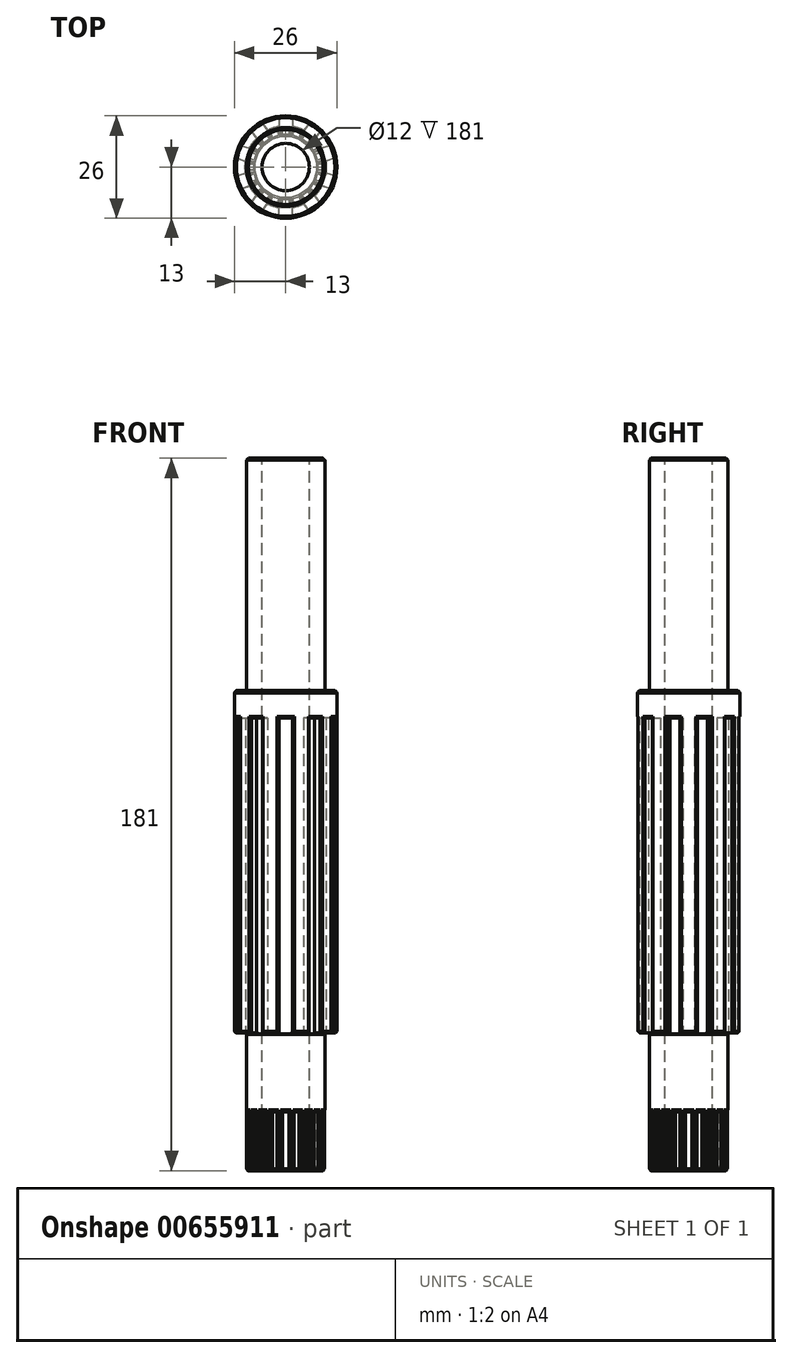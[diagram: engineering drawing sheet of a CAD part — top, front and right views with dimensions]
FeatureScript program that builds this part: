
annotation { "Feature Type Name" : "Feature", "Feature Type Description" : "" }
export const myFeature = defineFeature(function(context is Context, id is Id, definition is map)
    precondition{}
    {
        {
            var Q0;
            Q0=qCreatedBy(makeId("Top.planeOp"),FACE);
            var sketch = newSketch(context, id + "F0", { "sketchPlane" : qUnion([Q0])});
            skCircle(sketch, "E0", {"center": v(0, 0) * mm, "radius": 10 * mm});
            skSolve(sketch);
        }
        {
            var Q0;
            Q0=makeQuery(id+"F0.imprint","IMPRINT",FACE,{"disambiguationData":[TD([[makeQuery(id+"F0.imprint","IMPRINT",EDGE,{"derivedFrom":sQuery(id+"F0.wireOp",EDGE,"E0")}),1.0]])]});
            extrude(context, id + "F1", {"entities" : qUnion([Q0]), "oppositeDirection" : true, "depth" : 59 * mm, "offsetDistance" : 25 * mm});
        }
        {
            var Q0;
            Q0=makeQuery(id+"F1.opExtrude","CAP_FACE",FACE,{"disambiguationData":[OSD([sQuery(id+"F0.wireOp",EDGE,"E0")])],"isStart":false});
            var sketch = newSketch(context, id + "F2", { "sketchPlane" : qUnion([Q0])});
            skCircle(sketch, "E1", {"center": v(0, 0) * mm, "radius": 13 * mm});
            skSolve(sketch);
        }
        {
            var Q0;
            Q0=makeQuery(id+"F2.imprint","IMPRINT",FACE,{"disambiguationData":[TD([[makeQuery(id+"F2.imprint","IMPRINT",EDGE,{"derivedFrom":makeQuery(id+"F1.opExtrude","CAP_EDGE",EDGE,{"disambiguationData":[OSD([sQuery(id+"F0.wireOp",EDGE,"E0")])],"isStart":false})}),-1.0]])]});
            var Q1;
            Q1=makeQuery(id+"F2.imprint","IMPRINT",FACE,{"disambiguationData":[TD([[makeQuery(id+"F2.imprint","IMPRINT",EDGE,{"derivedFrom":sQuery(id+"F2.wireOp",EDGE,"E1")}),1.0]])]});
            var Q2;
            Q2=sQuery(id+"F2.wireOp",EDGE,"E1");
            extrude(context, id + "F3", {"entities" : qUnion([Q0, Q1]), "operationType" : NewBodyOperationType.ADD, "surfaceEntities" : qUnion([Q2]), "depth" : 87 * mm, "offsetDistance" : 25 * mm});
        }
        {
            var Q0;
            Q0=makeQuery(id+"F3.opExtrude","CAP_FACE",FACE,{"disambiguationData":[OSD([sQuery(id+"F2.wireOp",EDGE,"E1")])],"isStart":false});
            var sketch = newSketch(context, id + "F4", { "sketchPlane" : qUnion([Q0])});
            skLineSegment(sketch, "E2.bottom", {"start": v(1.73, 13.86) * mm, "end": v(-1.73, 13.86) * mm});
            skLineSegment(sketch, "E2.top", {"start": v(1.73, 10.15) * mm, "end": v(-1.73, 10.15) * mm});
            skLineSegment(sketch, "E2.left", {"start": v(1.73, 13.86) * mm, "end": v(1.73, 10.15) * mm});
            skLineSegment(sketch, "E2.right", {"start": v(-1.73, 13.86) * mm, "end": v(-1.73, 10.15) * mm});
            skPoint(sketch, "E2.middle", {"position": v(0, 12) * mm});
            skLineSegment(sketch, "E3.1.0", {"start": v(-9.54, 10.2) * mm, "end": v(-7.36, 7.2) * mm});
            skLineSegment(sketch, "E3.1.1", {"start": v(-6.75, 12.23) * mm, "end": v(-4.57, 9.23) * mm});
            skLineSegment(sketch, "E3.1.2", {"start": v(-4.57, 9.23) * mm, "end": v(-7.36, 7.2) * mm});
            skLineSegment(sketch, "E3.1.3", {"start": v(-6.75, 12.23) * mm, "end": v(-9.54, 10.2) * mm});
            skLineSegment(sketch, "E3.2.0", {"start": v(-13.72, 2.64) * mm, "end": v(-10.19, 1.5) * mm});
            skLineSegment(sketch, "E3.2.1", {"start": v(-12.65, 5.93) * mm, "end": v(-9.12, 4.78) * mm});
            skLineSegment(sketch, "E3.2.2", {"start": v(-9.12, 4.78) * mm, "end": v(-10.19, 1.5) * mm});
            skLineSegment(sketch, "E3.2.3", {"start": v(-12.65, 5.93) * mm, "end": v(-13.72, 2.64) * mm});
            skLineSegment(sketch, "E3.3.0", {"start": v(-12.65, -5.93) * mm, "end": v(-9.12, -4.78) * mm});
            skLineSegment(sketch, "E3.3.1", {"start": v(-13.72, -2.64) * mm, "end": v(-10.19, -1.5) * mm});
            skLineSegment(sketch, "E3.3.2", {"start": v(-10.19, -1.5) * mm, "end": v(-9.12, -4.78) * mm});
            skLineSegment(sketch, "E3.3.3", {"start": v(-13.72, -2.64) * mm, "end": v(-12.65, -5.93) * mm});
            skLineSegment(sketch, "E3.4.0", {"start": v(-6.75, -12.23) * mm, "end": v(-4.57, -9.23) * mm});
            skLineSegment(sketch, "E3.4.1", {"start": v(-9.54, -10.2) * mm, "end": v(-7.36, -7.2) * mm});
            skLineSegment(sketch, "E3.4.2", {"start": v(-7.36, -7.2) * mm, "end": v(-4.57, -9.23) * mm});
            skLineSegment(sketch, "E3.4.3", {"start": v(-9.54, -10.2) * mm, "end": v(-6.75, -12.23) * mm});
            skLineSegment(sketch, "E3.5.0", {"start": v(1.73, -13.86) * mm, "end": v(1.73, -10.15) * mm});
            skLineSegment(sketch, "E3.5.1", {"start": v(-1.73, -13.86) * mm, "end": v(-1.73, -10.15) * mm});
            skLineSegment(sketch, "E3.5.2", {"start": v(-1.73, -10.15) * mm, "end": v(1.73, -10.15) * mm});
            skLineSegment(sketch, "E3.5.3", {"start": v(-1.73, -13.86) * mm, "end": v(1.73, -13.86) * mm});
            skLineSegment(sketch, "E3.6.0", {"start": v(9.54, -10.2) * mm, "end": v(7.36, -7.2) * mm});
            skLineSegment(sketch, "E3.6.1", {"start": v(6.75, -12.23) * mm, "end": v(4.57, -9.23) * mm});
            skLineSegment(sketch, "E3.6.2", {"start": v(4.57, -9.23) * mm, "end": v(7.36, -7.2) * mm});
            skLineSegment(sketch, "E3.6.3", {"start": v(6.75, -12.23) * mm, "end": v(9.54, -10.2) * mm});
            skLineSegment(sketch, "E3.7.0", {"start": v(13.72, -2.64) * mm, "end": v(10.19, -1.5) * mm});
            skLineSegment(sketch, "E3.7.1", {"start": v(12.65, -5.93) * mm, "end": v(9.12, -4.78) * mm});
            skLineSegment(sketch, "E3.7.2", {"start": v(9.12, -4.78) * mm, "end": v(10.19, -1.5) * mm});
            skLineSegment(sketch, "E3.7.3", {"start": v(12.65, -5.93) * mm, "end": v(13.72, -2.64) * mm});
            skLineSegment(sketch, "E3.8.0", {"start": v(12.65, 5.93) * mm, "end": v(9.12, 4.78) * mm});
            skLineSegment(sketch, "E3.8.1", {"start": v(13.72, 2.64) * mm, "end": v(10.19, 1.5) * mm});
            skLineSegment(sketch, "E3.8.2", {"start": v(10.19, 1.5) * mm, "end": v(9.12, 4.78) * mm});
            skLineSegment(sketch, "E3.8.3", {"start": v(13.72, 2.64) * mm, "end": v(12.65, 5.93) * mm});
            skLineSegment(sketch, "E3.9.0", {"start": v(6.75, 12.23) * mm, "end": v(4.57, 9.23) * mm});
            skLineSegment(sketch, "E3.9.1", {"start": v(9.54, 10.2) * mm, "end": v(7.36, 7.2) * mm});
            skLineSegment(sketch, "E3.9.2", {"start": v(7.36, 7.2) * mm, "end": v(4.57, 9.23) * mm});
            skLineSegment(sketch, "E3.9.3", {"start": v(9.54, 10.2) * mm, "end": v(6.75, 12.23) * mm});
            skPoint(sketch, "E3.center", {"position": v(0, 0) * mm});
            skSolve(sketch);
        }
        {
            var Q0;
            {var subQ0=sQuery(id+"F4.wireOp",EDGE,"E3.1.2");Q0=makeQuery(id+"F4.imprint","IMPRINT",FACE,{"disambiguationData":[TD([[makeQuery(id+"F4.imprint","IMPRINT",EDGE,{"derivedFrom":subQ0}),-1.0]])]});}
            var Q1;
            {var subQ0=sQuery(id+"F4.wireOp",EDGE,"E3.2.2");Q1=makeQuery(id+"F4.imprint","IMPRINT",FACE,{"disambiguationData":[TD([[makeQuery(id+"F4.imprint","IMPRINT",EDGE,{"derivedFrom":subQ0}),-1.0]])]});}
            var Q2;
            {var subQ0=sQuery(id+"F4.wireOp",EDGE,"E3.3.2");Q2=makeQuery(id+"F4.imprint","IMPRINT",FACE,{"disambiguationData":[TD([[makeQuery(id+"F4.imprint","IMPRINT",EDGE,{"derivedFrom":subQ0}),-1.0]])]});}
            var Q3;
            {var subQ0=sQuery(id+"F4.wireOp",EDGE,"E3.4.2");Q3=makeQuery(id+"F4.imprint","IMPRINT",FACE,{"disambiguationData":[TD([[makeQuery(id+"F4.imprint","IMPRINT",EDGE,{"derivedFrom":subQ0}),-1.0]])]});}
            var Q4;
            {var subQ0=sQuery(id+"F4.wireOp",EDGE,"E3.5.2");Q4=makeQuery(id+"F4.imprint","IMPRINT",FACE,{"disambiguationData":[TD([[makeQuery(id+"F4.imprint","IMPRINT",EDGE,{"derivedFrom":subQ0}),-1.0]])]});}
            var Q5;
            {var subQ0=sQuery(id+"F4.wireOp",EDGE,"E3.6.2");Q5=makeQuery(id+"F4.imprint","IMPRINT",FACE,{"disambiguationData":[TD([[makeQuery(id+"F4.imprint","IMPRINT",EDGE,{"derivedFrom":subQ0}),-1.0]])]});}
            var Q6;
            {var subQ0=sQuery(id+"F4.wireOp",EDGE,"E3.7.2");Q6=makeQuery(id+"F4.imprint","IMPRINT",FACE,{"disambiguationData":[TD([[makeQuery(id+"F4.imprint","IMPRINT",EDGE,{"derivedFrom":subQ0}),-1.0]])]});}
            var Q7;
            {var subQ0=sQuery(id+"F4.wireOp",EDGE,"E3.8.2");Q7=makeQuery(id+"F4.imprint","IMPRINT",FACE,{"disambiguationData":[TD([[makeQuery(id+"F4.imprint","IMPRINT",EDGE,{"derivedFrom":subQ0}),-1.0]])]});}
            var Q8;
            {var subQ0=sQuery(id+"F4.wireOp",EDGE,"E3.9.2");Q8=makeQuery(id+"F4.imprint","IMPRINT",FACE,{"disambiguationData":[TD([[makeQuery(id+"F4.imprint","IMPRINT",EDGE,{"derivedFrom":subQ0}),-1.0]])]});}
            var Q9;
            {var subQ0=sQuery(id+"F4.wireOp",EDGE,"E2.top");Q9=makeQuery(id+"F4.imprint","IMPRINT",FACE,{"disambiguationData":[TD([[makeQuery(id+"F4.imprint","IMPRINT",EDGE,{"derivedFrom":subQ0}),-1.0]])]});}
            extrude(context, id + "F5", {"entities" : qUnion([Q0, Q1, Q2, Q3, Q4, Q5, Q6, Q7, Q8, Q9]), "operationType" : NewBodyOperationType.REMOVE, "oppositeDirection" : true, "depth" : 80 * mm, "offsetDistance" : 25 * mm});
        }
        {
            var Q0;
            Q0=makeQuery(id+"F3.opExtrude","CAP_FACE",FACE,{"disambiguationData":[OSD([sQuery(id+"F2.wireOp",EDGE,"E1")])],"isStart":false});
            var sketch = newSketch(context, id + "F6", { "sketchPlane" : qUnion([Q0])});
            skCircle(sketch, "E4", {"center": v(0, 0) * mm, "radius": 10 * mm});
            skSolve(sketch);
        }
        {
            var Q0;
            Q0=makeQuery(id+"F6.imprint","IMPRINT",FACE,{"disambiguationData":[TD([[makeQuery(id+"F6.imprint","IMPRINT",EDGE,{"derivedFrom":sQuery(id+"F6.wireOp",EDGE,"E4")}),1.0]])]});
            extrude(context, id + "F7", {"entities" : qUnion([Q0]), "operationType" : NewBodyOperationType.ADD, "depth" : 35 * mm, "offsetDistance" : 25 * mm});
        }
        {
            var Q0;
            Q0=makeQuery(id+"F7.opExtrude","CAP_FACE",FACE,{"disambiguationData":[OSD([sQuery(id+"F6.wireOp",EDGE,"E4")])],"isStart":false});
            var sketch = newSketch(context, id + "F8", { "sketchPlane" : qUnion([Q0])});
            skLineSegment(sketch, "E5.bottom", {"start": v(0.84, 10.38) * mm, "end": v(-0.84, 10.38) * mm});
            skLineSegment(sketch, "E5.top", {"start": v(0.84, 8.18) * mm, "end": v(-0.84, 8.18) * mm});
            skLineSegment(sketch, "E5.left", {"start": v(0.84, 10.38) * mm, "end": v(0.84, 8.18) * mm});
            skLineSegment(sketch, "E5.right", {"start": v(-0.84, 10.38) * mm, "end": v(-0.84, 8.18) * mm});
            skPoint(sketch, "E5.middle", {"position": v(0, 9.28) * mm});
            skLineSegment(sketch, "E6.1.0", {"start": v(-2.4, 10.13) * mm, "end": v(-1.72, 8.04) * mm});
            skLineSegment(sketch, "E6.1.1", {"start": v(-1.72, 8.04) * mm, "end": v(-3.33, 7.52) * mm});
            skLineSegment(sketch, "E6.1.2", {"start": v(-4.01, 9.6) * mm, "end": v(-3.33, 7.52) * mm});
            skLineSegment(sketch, "E6.1.3", {"start": v(-2.4, 10.13) * mm, "end": v(-4.01, 9.6) * mm});
            skLineSegment(sketch, "E6.2.0", {"start": v(-5.42, 8.9) * mm, "end": v(-4.12, 7.11) * mm});
            skLineSegment(sketch, "E6.2.1", {"start": v(-4.12, 7.11) * mm, "end": v(-5.5, 6.12) * mm});
            skLineSegment(sketch, "E6.2.2", {"start": v(-6.78, 7.9) * mm, "end": v(-5.5, 6.12) * mm});
            skLineSegment(sketch, "E6.2.3", {"start": v(-5.42, 8.9) * mm, "end": v(-6.78, 7.9) * mm});
            skLineSegment(sketch, "E6.3.0", {"start": v(-7.9, 6.78) * mm, "end": v(-6.12, 5.5) * mm});
            skLineSegment(sketch, "E6.3.1", {"start": v(-6.12, 5.5) * mm, "end": v(-7.11, 4.12) * mm});
            skLineSegment(sketch, "E6.3.2", {"start": v(-8.9, 5.42) * mm, "end": v(-7.11, 4.12) * mm});
            skLineSegment(sketch, "E6.3.3", {"start": v(-7.9, 6.78) * mm, "end": v(-8.9, 5.42) * mm});
            skLineSegment(sketch, "E6.4.0", {"start": v(-9.6, 4.01) * mm, "end": v(-7.52, 3.33) * mm});
            skLineSegment(sketch, "E6.4.1", {"start": v(-7.52, 3.33) * mm, "end": v(-8.04, 1.72) * mm});
            skLineSegment(sketch, "E6.4.2", {"start": v(-10.13, 2.4) * mm, "end": v(-8.04, 1.72) * mm});
            skLineSegment(sketch, "E6.4.3", {"start": v(-9.6, 4.01) * mm, "end": v(-10.13, 2.4) * mm});
            skLineSegment(sketch, "E6.5.0", {"start": v(-10.38, 0.84) * mm, "end": v(-8.18, 0.84) * mm});
            skLineSegment(sketch, "E6.5.1", {"start": v(-8.18, 0.84) * mm, "end": v(-8.18, -0.84) * mm});
            skLineSegment(sketch, "E6.5.2", {"start": v(-10.38, -0.84) * mm, "end": v(-8.18, -0.84) * mm});
            skLineSegment(sketch, "E6.5.3", {"start": v(-10.38, 0.84) * mm, "end": v(-10.38, -0.84) * mm});
            skLineSegment(sketch, "E6.6.0", {"start": v(-10.13, -2.4) * mm, "end": v(-8.04, -1.72) * mm});
            skLineSegment(sketch, "E6.6.1", {"start": v(-8.04, -1.72) * mm, "end": v(-7.52, -3.33) * mm});
            skLineSegment(sketch, "E6.6.2", {"start": v(-9.6, -4.01) * mm, "end": v(-7.52, -3.33) * mm});
            skLineSegment(sketch, "E6.6.3", {"start": v(-10.13, -2.4) * mm, "end": v(-9.6, -4.01) * mm});
            skLineSegment(sketch, "E6.7.0", {"start": v(-8.9, -5.42) * mm, "end": v(-7.11, -4.12) * mm});
            skLineSegment(sketch, "E6.7.1", {"start": v(-7.11, -4.12) * mm, "end": v(-6.12, -5.5) * mm});
            skLineSegment(sketch, "E6.7.2", {"start": v(-7.9, -6.78) * mm, "end": v(-6.12, -5.5) * mm});
            skLineSegment(sketch, "E6.7.3", {"start": v(-8.9, -5.42) * mm, "end": v(-7.9, -6.78) * mm});
            skLineSegment(sketch, "E6.8.0", {"start": v(-6.78, -7.9) * mm, "end": v(-5.5, -6.12) * mm});
            skLineSegment(sketch, "E6.8.1", {"start": v(-5.5, -6.12) * mm, "end": v(-4.12, -7.11) * mm});
            skLineSegment(sketch, "E6.8.2", {"start": v(-5.42, -8.9) * mm, "end": v(-4.12, -7.11) * mm});
            skLineSegment(sketch, "E6.8.3", {"start": v(-6.78, -7.9) * mm, "end": v(-5.42, -8.9) * mm});
            skLineSegment(sketch, "E6.9.0", {"start": v(-4.01, -9.6) * mm, "end": v(-3.33, -7.52) * mm});
            skLineSegment(sketch, "E6.9.1", {"start": v(-3.33, -7.52) * mm, "end": v(-1.72, -8.04) * mm});
            skLineSegment(sketch, "E6.9.2", {"start": v(-2.4, -10.13) * mm, "end": v(-1.72, -8.04) * mm});
            skLineSegment(sketch, "E6.9.3", {"start": v(-4.01, -9.6) * mm, "end": v(-2.4, -10.13) * mm});
            skLineSegment(sketch, "E6.10.0", {"start": v(-0.84, -10.38) * mm, "end": v(-0.84, -8.18) * mm});
            skLineSegment(sketch, "E6.10.1", {"start": v(-0.84, -8.18) * mm, "end": v(0.84, -8.18) * mm});
            skLineSegment(sketch, "E6.10.2", {"start": v(0.84, -10.38) * mm, "end": v(0.84, -8.18) * mm});
            skLineSegment(sketch, "E6.10.3", {"start": v(-0.84, -10.38) * mm, "end": v(0.84, -10.38) * mm});
            skLineSegment(sketch, "E6.11.0", {"start": v(2.4, -10.13) * mm, "end": v(1.72, -8.04) * mm});
            skLineSegment(sketch, "E6.11.1", {"start": v(1.72, -8.04) * mm, "end": v(3.33, -7.52) * mm});
            skLineSegment(sketch, "E6.11.2", {"start": v(4.01, -9.6) * mm, "end": v(3.33, -7.52) * mm});
            skLineSegment(sketch, "E6.11.3", {"start": v(2.4, -10.13) * mm, "end": v(4.01, -9.6) * mm});
            skLineSegment(sketch, "E6.12.0", {"start": v(5.42, -8.9) * mm, "end": v(4.12, -7.11) * mm});
            skLineSegment(sketch, "E6.12.1", {"start": v(4.12, -7.11) * mm, "end": v(5.5, -6.12) * mm});
            skLineSegment(sketch, "E6.12.2", {"start": v(6.78, -7.9) * mm, "end": v(5.5, -6.12) * mm});
            skLineSegment(sketch, "E6.12.3", {"start": v(5.42, -8.9) * mm, "end": v(6.78, -7.9) * mm});
            skLineSegment(sketch, "E6.13.0", {"start": v(7.9, -6.78) * mm, "end": v(6.12, -5.5) * mm});
            skLineSegment(sketch, "E6.13.1", {"start": v(6.12, -5.5) * mm, "end": v(7.11, -4.12) * mm});
            skLineSegment(sketch, "E6.13.2", {"start": v(8.9, -5.42) * mm, "end": v(7.11, -4.12) * mm});
            skLineSegment(sketch, "E6.13.3", {"start": v(7.9, -6.78) * mm, "end": v(8.9, -5.42) * mm});
            skLineSegment(sketch, "E6.14.0", {"start": v(9.6, -4.01) * mm, "end": v(7.52, -3.33) * mm});
            skLineSegment(sketch, "E6.14.1", {"start": v(7.52, -3.33) * mm, "end": v(8.04, -1.72) * mm});
            skLineSegment(sketch, "E6.14.2", {"start": v(10.13, -2.4) * mm, "end": v(8.04, -1.72) * mm});
            skLineSegment(sketch, "E6.14.3", {"start": v(9.6, -4.01) * mm, "end": v(10.13, -2.4) * mm});
            skLineSegment(sketch, "E6.15.0", {"start": v(10.38, -0.84) * mm, "end": v(8.18, -0.84) * mm});
            skLineSegment(sketch, "E6.15.1", {"start": v(8.18, -0.84) * mm, "end": v(8.18, 0.84) * mm});
            skLineSegment(sketch, "E6.15.2", {"start": v(10.38, 0.84) * mm, "end": v(8.18, 0.84) * mm});
            skLineSegment(sketch, "E6.15.3", {"start": v(10.38, -0.84) * mm, "end": v(10.38, 0.84) * mm});
            skLineSegment(sketch, "E6.16.0", {"start": v(10.13, 2.4) * mm, "end": v(8.04, 1.72) * mm});
            skLineSegment(sketch, "E6.16.1", {"start": v(8.04, 1.72) * mm, "end": v(7.52, 3.33) * mm});
            skLineSegment(sketch, "E6.16.2", {"start": v(9.6, 4.01) * mm, "end": v(7.52, 3.33) * mm});
            skLineSegment(sketch, "E6.16.3", {"start": v(10.13, 2.4) * mm, "end": v(9.6, 4.01) * mm});
            skLineSegment(sketch, "E6.17.0", {"start": v(8.9, 5.42) * mm, "end": v(7.11, 4.12) * mm});
            skLineSegment(sketch, "E6.17.1", {"start": v(7.11, 4.12) * mm, "end": v(6.12, 5.5) * mm});
            skLineSegment(sketch, "E6.17.2", {"start": v(7.9, 6.78) * mm, "end": v(6.12, 5.5) * mm});
            skLineSegment(sketch, "E6.17.3", {"start": v(8.9, 5.42) * mm, "end": v(7.9, 6.78) * mm});
            skLineSegment(sketch, "E6.18.0", {"start": v(6.78, 7.9) * mm, "end": v(5.5, 6.12) * mm});
            skLineSegment(sketch, "E6.18.1", {"start": v(5.5, 6.12) * mm, "end": v(4.12, 7.11) * mm});
            skLineSegment(sketch, "E6.18.2", {"start": v(5.42, 8.9) * mm, "end": v(4.12, 7.11) * mm});
            skLineSegment(sketch, "E6.18.3", {"start": v(6.78, 7.9) * mm, "end": v(5.42, 8.9) * mm});
            skLineSegment(sketch, "E6.19.0", {"start": v(4.01, 9.6) * mm, "end": v(3.33, 7.52) * mm});
            skLineSegment(sketch, "E6.19.1", {"start": v(3.33, 7.52) * mm, "end": v(1.72, 8.04) * mm});
            skLineSegment(sketch, "E6.19.2", {"start": v(2.4, 10.13) * mm, "end": v(1.72, 8.04) * mm});
            skLineSegment(sketch, "E6.19.3", {"start": v(4.01, 9.6) * mm, "end": v(2.4, 10.13) * mm});
            skPoint(sketch, "E6.center", {"position": v(0, 0) * mm});
            skSolve(sketch);
        }
        {
            var Q0;
            {var subQ0=sQuery(id+"F8.wireOp",EDGE,"E6.3.1");Q0=makeQuery(id+"F8.imprint","IMPRINT",FACE,{"disambiguationData":[TD([[makeQuery(id+"F8.imprint","IMPRINT",EDGE,{"derivedFrom":subQ0}),-1.0]])]});}
            var Q1;
            {var subQ0=sQuery(id+"F8.wireOp",EDGE,"E6.2.1");Q1=makeQuery(id+"F8.imprint","IMPRINT",FACE,{"disambiguationData":[TD([[makeQuery(id+"F8.imprint","IMPRINT",EDGE,{"derivedFrom":subQ0}),-1.0]])]});}
            var Q2;
            {var subQ0=sQuery(id+"F8.wireOp",EDGE,"E6.1.1");Q2=makeQuery(id+"F8.imprint","IMPRINT",FACE,{"disambiguationData":[TD([[makeQuery(id+"F8.imprint","IMPRINT",EDGE,{"derivedFrom":subQ0}),-1.0]])]});}
            var Q3;
            {var subQ0=sQuery(id+"F8.wireOp",EDGE,"E5.top");Q3=makeQuery(id+"F8.imprint","IMPRINT",FACE,{"disambiguationData":[TD([[makeQuery(id+"F8.imprint","IMPRINT",EDGE,{"derivedFrom":subQ0}),-1.0]])]});}
            var Q4;
            {var subQ0=sQuery(id+"F8.wireOp",EDGE,"E6.19.1");Q4=makeQuery(id+"F8.imprint","IMPRINT",FACE,{"disambiguationData":[TD([[makeQuery(id+"F8.imprint","IMPRINT",EDGE,{"derivedFrom":subQ0}),-1.0]])]});}
            var Q5;
            {var subQ0=sQuery(id+"F8.wireOp",EDGE,"E6.18.1");Q5=makeQuery(id+"F8.imprint","IMPRINT",FACE,{"disambiguationData":[TD([[makeQuery(id+"F8.imprint","IMPRINT",EDGE,{"derivedFrom":subQ0}),-1.0]])]});}
            var Q6;
            {var subQ0=sQuery(id+"F8.wireOp",EDGE,"E6.17.1");Q6=makeQuery(id+"F8.imprint","IMPRINT",FACE,{"disambiguationData":[TD([[makeQuery(id+"F8.imprint","IMPRINT",EDGE,{"derivedFrom":subQ0}),-1.0]])]});}
            var Q7;
            {var subQ0=sQuery(id+"F8.wireOp",EDGE,"E6.16.1");Q7=makeQuery(id+"F8.imprint","IMPRINT",FACE,{"disambiguationData":[TD([[makeQuery(id+"F8.imprint","IMPRINT",EDGE,{"derivedFrom":subQ0}),-1.0]])]});}
            var Q8;
            {var subQ0=sQuery(id+"F8.wireOp",EDGE,"E6.15.1");Q8=makeQuery(id+"F8.imprint","IMPRINT",FACE,{"disambiguationData":[TD([[makeQuery(id+"F8.imprint","IMPRINT",EDGE,{"derivedFrom":subQ0}),-1.0]])]});}
            var Q9;
            {var subQ0=sQuery(id+"F8.wireOp",EDGE,"E6.14.1");Q9=makeQuery(id+"F8.imprint","IMPRINT",FACE,{"disambiguationData":[TD([[makeQuery(id+"F8.imprint","IMPRINT",EDGE,{"derivedFrom":subQ0}),-1.0]])]});}
            var Q10;
            {var subQ0=sQuery(id+"F8.wireOp",EDGE,"E6.13.1");Q10=makeQuery(id+"F8.imprint","IMPRINT",FACE,{"disambiguationData":[TD([[makeQuery(id+"F8.imprint","IMPRINT",EDGE,{"derivedFrom":subQ0}),-1.0]])]});}
            var Q11;
            {var subQ0=sQuery(id+"F8.wireOp",EDGE,"E6.12.1");Q11=makeQuery(id+"F8.imprint","IMPRINT",FACE,{"disambiguationData":[TD([[makeQuery(id+"F8.imprint","IMPRINT",EDGE,{"derivedFrom":subQ0}),-1.0]])]});}
            var Q12;
            {var subQ0=sQuery(id+"F8.wireOp",EDGE,"E6.11.1");Q12=makeQuery(id+"F8.imprint","IMPRINT",FACE,{"disambiguationData":[TD([[makeQuery(id+"F8.imprint","IMPRINT",EDGE,{"derivedFrom":subQ0}),-1.0]])]});}
            var Q13;
            {var subQ0=sQuery(id+"F8.wireOp",EDGE,"E6.10.1");Q13=makeQuery(id+"F8.imprint","IMPRINT",FACE,{"disambiguationData":[TD([[makeQuery(id+"F8.imprint","IMPRINT",EDGE,{"derivedFrom":subQ0}),-1.0]])]});}
            var Q14;
            {var subQ0=sQuery(id+"F8.wireOp",EDGE,"E6.9.1");Q14=makeQuery(id+"F8.imprint","IMPRINT",FACE,{"disambiguationData":[TD([[makeQuery(id+"F8.imprint","IMPRINT",EDGE,{"derivedFrom":subQ0}),-1.0]])]});}
            var Q15;
            {var subQ0=sQuery(id+"F8.wireOp",EDGE,"E6.8.1");Q15=makeQuery(id+"F8.imprint","IMPRINT",FACE,{"disambiguationData":[TD([[makeQuery(id+"F8.imprint","IMPRINT",EDGE,{"derivedFrom":subQ0}),-1.0]])]});}
            var Q16;
            {var subQ0=sQuery(id+"F8.wireOp",EDGE,"E6.7.1");Q16=makeQuery(id+"F8.imprint","IMPRINT",FACE,{"disambiguationData":[TD([[makeQuery(id+"F8.imprint","IMPRINT",EDGE,{"derivedFrom":subQ0}),-1.0]])]});}
            var Q17;
            {var subQ0=sQuery(id+"F8.wireOp",EDGE,"E6.6.1");Q17=makeQuery(id+"F8.imprint","IMPRINT",FACE,{"disambiguationData":[TD([[makeQuery(id+"F8.imprint","IMPRINT",EDGE,{"derivedFrom":subQ0}),-1.0]])]});}
            var Q18;
            {var subQ0=sQuery(id+"F8.wireOp",EDGE,"E6.5.1");Q18=makeQuery(id+"F8.imprint","IMPRINT",FACE,{"disambiguationData":[TD([[makeQuery(id+"F8.imprint","IMPRINT",EDGE,{"derivedFrom":subQ0}),-1.0]])]});}
            var Q19;
            {var subQ0=sQuery(id+"F8.wireOp",EDGE,"E6.4.1");Q19=makeQuery(id+"F8.imprint","IMPRINT",FACE,{"disambiguationData":[TD([[makeQuery(id+"F8.imprint","IMPRINT",EDGE,{"derivedFrom":subQ0}),-1.0]])]});}
            extrude(context, id + "F9", {"entities" : qUnion([Q0, Q1, Q2, Q3, Q4, Q5, Q6, Q7, Q8, Q9, Q10, Q11, Q12, Q13, Q14, Q15, Q16, Q17, Q18, Q19]), "operationType" : NewBodyOperationType.REMOVE, "oppositeDirection" : true, "depth" : 15 * mm, "offsetDistance" : 25 * mm});
        }
        {
            var Q0;
            Q0=makeQuery(id+"F1.opExtrude","CAP_EDGE",EDGE,{"disambiguationData":[OSD([sQuery(id+"F0.wireOp",EDGE,"E0")])],"isStart":true});
            var Q1;
            Q1=makeQuery(id+"F3.opExtrude","CAP_EDGE",EDGE,{"disambiguationData":[OSD([sQuery(id+"F2.wireOp",EDGE,"E1")])],"isStart":true});
            chamfer(context, id + "F10", {"entities" : qUnion([Q0, Q1]), "width" : .5 * mm, "tangentPropagation" : true});
        }
        {
            var Q0;
            Q0=makeQuery(id+"F7.opExtrude","CAP_FACE",FACE,{"disambiguationData":[OSD([sQuery(id+"F6.wireOp",EDGE,"E4")])],"isStart":false});
            var Q1;
            Q1=makeQuery(id+"F3.opExtrude","SWEPT_FACE",FACE,{"disambiguationData":[OSD([sQuery(id+"F2.wireOp",EDGE,"E1")])]});
            var Q2;
            Q2=makeQuery(id+"F7.opExtrude","SWEPT_FACE",FACE,{"disambiguationData":[OSD([sQuery(id+"F6.wireOp",EDGE,"E4")])]});
            chamfer(context, id + "F11", {"entities" : qUnion([Q0, Q1, Q2]), "width" : .4 * mm, "tangentPropagation" : true});
        }
        {
            var Q0;
            Q0=makeQuery(id+"F1.opExtrude","CAP_FACE",FACE,{"disambiguationData":[OSD([sQuery(id+"F0.wireOp",EDGE,"E0")])],"isStart":true});
            var sketch = newSketch(context, id + "F12", { "sketchPlane" : qUnion([Q0])});
            skPoint(sketch, "E7", {"position": v(0, 0) * mm});
            skCircle(sketch, "E8", {"center": v(0, 0) * mm, "radius": 6 * mm});
            skSolve(sketch);
        }
        {
            var Q0;
            Q0=makeQuery(id+"F12.imprint","IMPRINT",FACE,{"disambiguationData":[TD([[makeQuery(id+"F12.imprint","IMPRINT",EDGE,{"derivedFrom":sQuery(id+"F12.wireOp",EDGE,"E8")}),1.0]])]});
            extrude(context, id + "F13", {"entities" : qUnion([Q0]), "operationType" : NewBodyOperationType.REMOVE, "oppositeDirection" : true, "depth" : 182 * mm, "offsetDistance" : 25 * mm});
        }
    });
